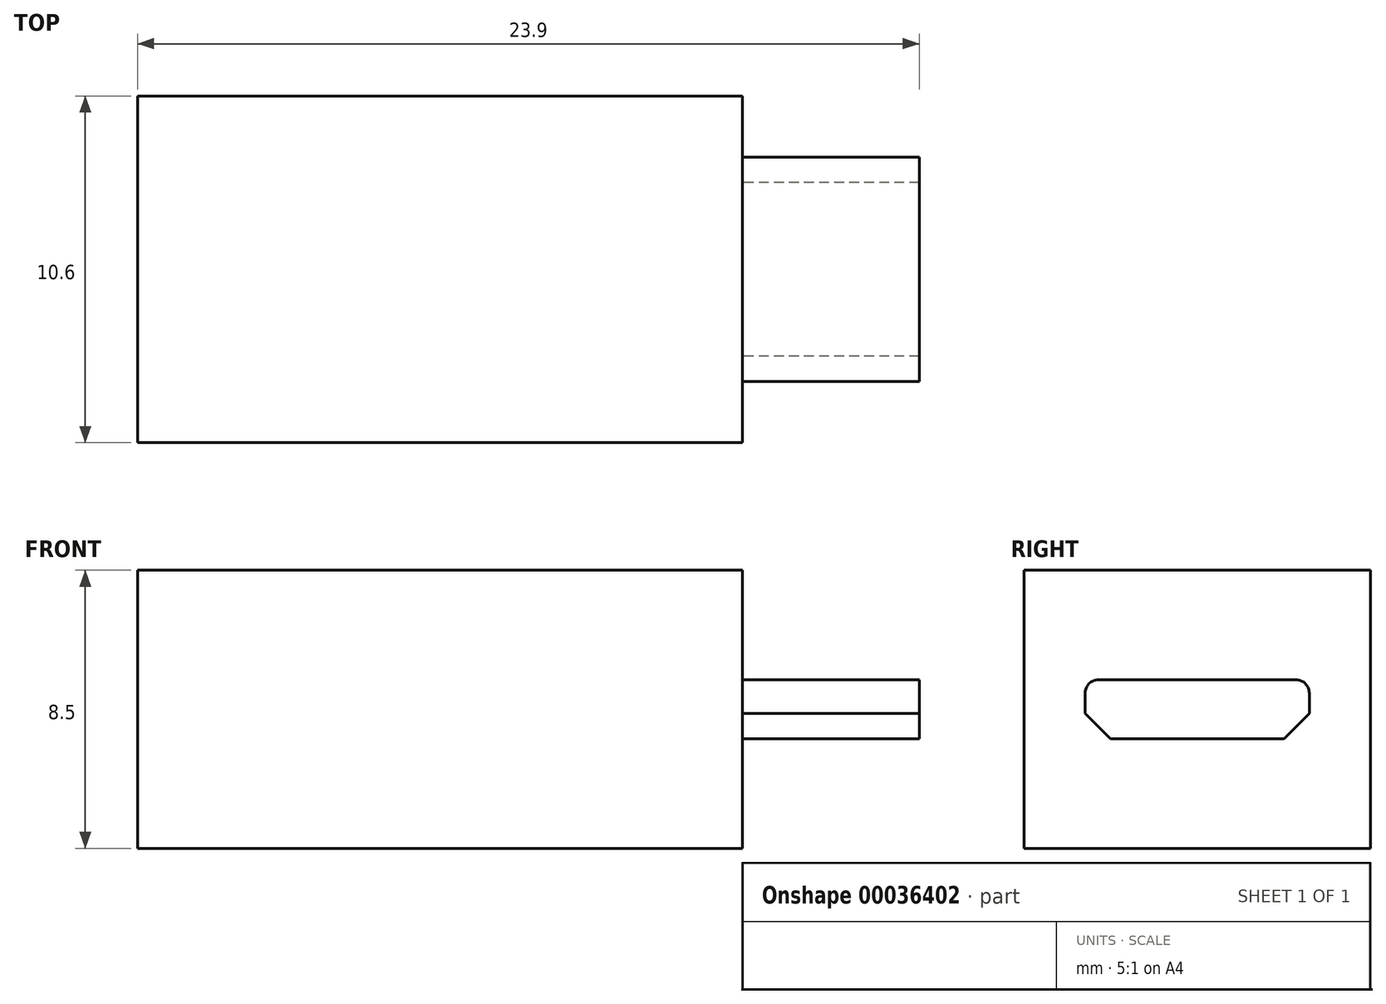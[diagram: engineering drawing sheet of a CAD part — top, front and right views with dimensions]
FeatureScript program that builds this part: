
annotation { "Feature Type Name" : "Feature", "Feature Type Description" : "" }
export const myFeature = defineFeature(function(context is Context, id is Id, definition is map)
    precondition{}
    {
        {
            var Q0;
            Q0=qCreatedBy(makeId("Top.planeOp"),FACE);
            var sketch = newSketch(context, id + "F0", { "sketchPlane" : qUnion([Q0])});
            skLineSegment(sketch, "E0.bottom", {"start": v(0, 0) * mm, "end": v(18.5, 0) * mm});
            skLineSegment(sketch, "E0.top", {"start": v(0, 10.6) * mm, "end": v(18.5, 10.6) * mm});
            skLineSegment(sketch, "E0.left", {"start": v(0, 0) * mm, "end": v(0, 10.6) * mm});
            skLineSegment(sketch, "E0.right", {"start": v(18.5, 0) * mm, "end": v(18.5, 10.6) * mm});
            skSolve(sketch);
        }
        {
            var Q0;
            Q0=qSketchRegion(id+"F0",true);
            extrude(context, id + "F1", {"entities" : qUnion([Q0]), "depth" : 8.5 * mm});
        }
        {
            var Q0;
            Q0=makeQuery(id+"F1.opExtrude","SWEPT_FACE",FACE,{"disambiguationData":[OSD([sQuery(id+"F0.wireOp",EDGE,"E0.right")])]});
            var sketch = newSketch(context, id + "F2", { "sketchPlane" : qUnion([Q0])});
            skLineSegment(sketch, "E1", {"start": v(2.27, 5.15) * mm, "end": v(8.32, 5.15) * mm});
            skLineSegment(sketch, "E2", {"start": v(8.72, 4.75) * mm, "end": v(8.72, 4.12) * mm});
            skLineSegment(sketch, "E3", {"start": v(8.72, 4.12) * mm, "end": v(7.95, 3.35) * mm});
            skLineSegment(sketch, "E4", {"start": v(7.95, 3.35) * mm, "end": v(2.65, 3.35) * mm});
            skLineSegment(sketch, "E5", {"start": v(2.65, 3.35) * mm, "end": v(1.87, 4.12) * mm});
            skLineSegment(sketch, "E6", {"start": v(1.87, 4.12) * mm, "end": v(1.87, 4.75) * mm});
            skPoint(sketch, "E7.visualSharp", {"position": v(1.87, 5.15) * mm});
            skArc(sketch, "E7.filletArc", {"start": v(2.27, 5.15) * mm, "mid": v(2, 5.03) * mm, "end": v(1.87, 4.75) * mm});
            skPoint(sketch, "E8.visualSharp", {"position": v(8.72, 5.15) * mm});
            skArc(sketch, "E8.filletArc", {"start": v(8.72, 4.75) * mm, "mid": v(8.6, 5.03) * mm, "end": v(8.32, 5.15) * mm});
            skSolve(sketch);
        }
        {
            var Q0;
            Q0=makeQuery(id+"F2.imprint","IMPRINT",FACE,{"disambiguationData":[TD([[makeQuery(id+"F2.imprint","IMPRINT",EDGE,{"derivedFrom":sQuery(id+"F2.wireOp",EDGE,"E1")}),-1.0]])]});
            extrude(context, id + "F3", {"entities" : qUnion([Q0]), "operationType" : NewBodyOperationType.ADD, "depth" : 5.4 * mm});
        }
    });
